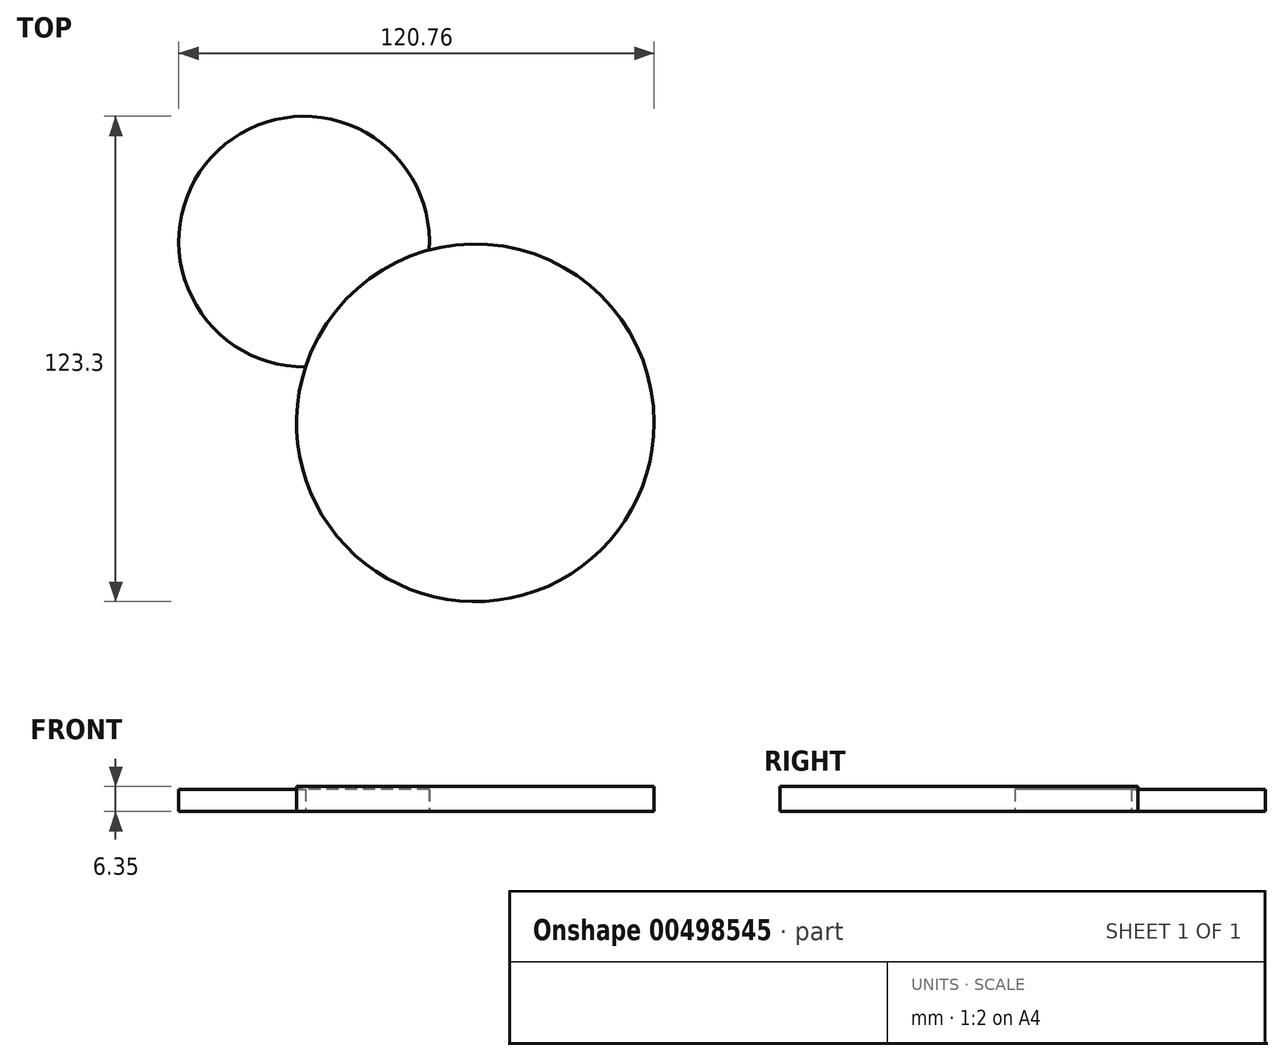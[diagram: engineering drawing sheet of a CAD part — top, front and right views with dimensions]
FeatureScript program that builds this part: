
annotation { "Feature Type Name" : "Feature", "Feature Type Description" : "" }
export const myFeature = defineFeature(function(context is Context, id is Id, definition is map)
    precondition{}
    {
        {
            var Q0;
            Q0=qCreatedBy(makeId("Top.planeOp"),FACE);
            var sketch = newSketch(context, id + "F0", { "sketchPlane" : qUnion([Q0])});
            skCircle(sketch, "E0", {"center": v(0, 0) * mm, "radius": 45.43 * mm});
            skSolve(sketch);
        }
        {
            var Q0;
            Q0=makeQuery(id+"F0.imprint","IMPRINT",FACE,{"disambiguationData":[TD([[makeQuery(id+"F0.imprint","IMPRINT",EDGE,{"derivedFrom":sQuery(id+"F0.wireOp",EDGE,"E0")}),1.0]])]});
            extrude(context, id + "F1", {"entities" : qUnion([Q0]), "depth" : 6.35 * mm});
        }
        {
            var Q0;
            Q0=qCreatedBy(makeId("Top.planeOp"),FACE);
            var sketch = newSketch(context, id + "F2", { "sketchPlane" : qUnion([Q0])});
            skCircle(sketch, "E1", {"center": v(-43.5, 46.04) * mm, "radius": 31.83 * mm});
            skSolve(sketch);
        }
        {
            var Q0;
            Q0=makeQuery(id+"F2.imprint","IMPRINT",FACE,{"disambiguationData":[TD([[makeQuery(id+"F2.imprint","IMPRINT",EDGE,{"derivedFrom":sQuery(id+"F2.wireOp",EDGE,"E1")}),1.0]])]});
            extrude(context, id + "F3", {"entities" : qUnion([Q0]), "operationType" : NewBodyOperationType.ADD, "depth" : 5.6 * mm});
        }
        {
            var Q0;
            Q0=qCreatedBy(makeId("Top.planeOp"),FACE);
            var sketch = newSketch(context, id + "F4", { "sketchPlane" : qUnion([Q0])});
            skFitSpline(sketch, "E2", {"points": [v(10.43, -77.9) * mm, v(18.22, -65.75) * mm, v(40.31, -58.83) * mm, v(43.83, -41.11) * mm, v(53.08, -35.77) * mm, v(67.73, -26.95) * mm, v(64.28, -2.66) * mm, v(74.5, 12) * mm, v(73.37, 34.7) * mm, v(88.85, 30.5) * mm, v(88.58, 30.34) * mm], "startDerivative": vector(44.62, 149.62) * mm, "endDerivative": vector(-33.36, -4.55) * mm});
            skSolve(sketch);
        }
        {
            var Q0;
            Q0=sQuery(id+"F4.wireOp",EDGE,"E2");
            extrude(context, id + "F5", {"bodyType" : ToolBodyType.SURFACE, "surfaceEntities" : qUnion([Q0]), "depth" : 82.04 * mm});
        }
    });
